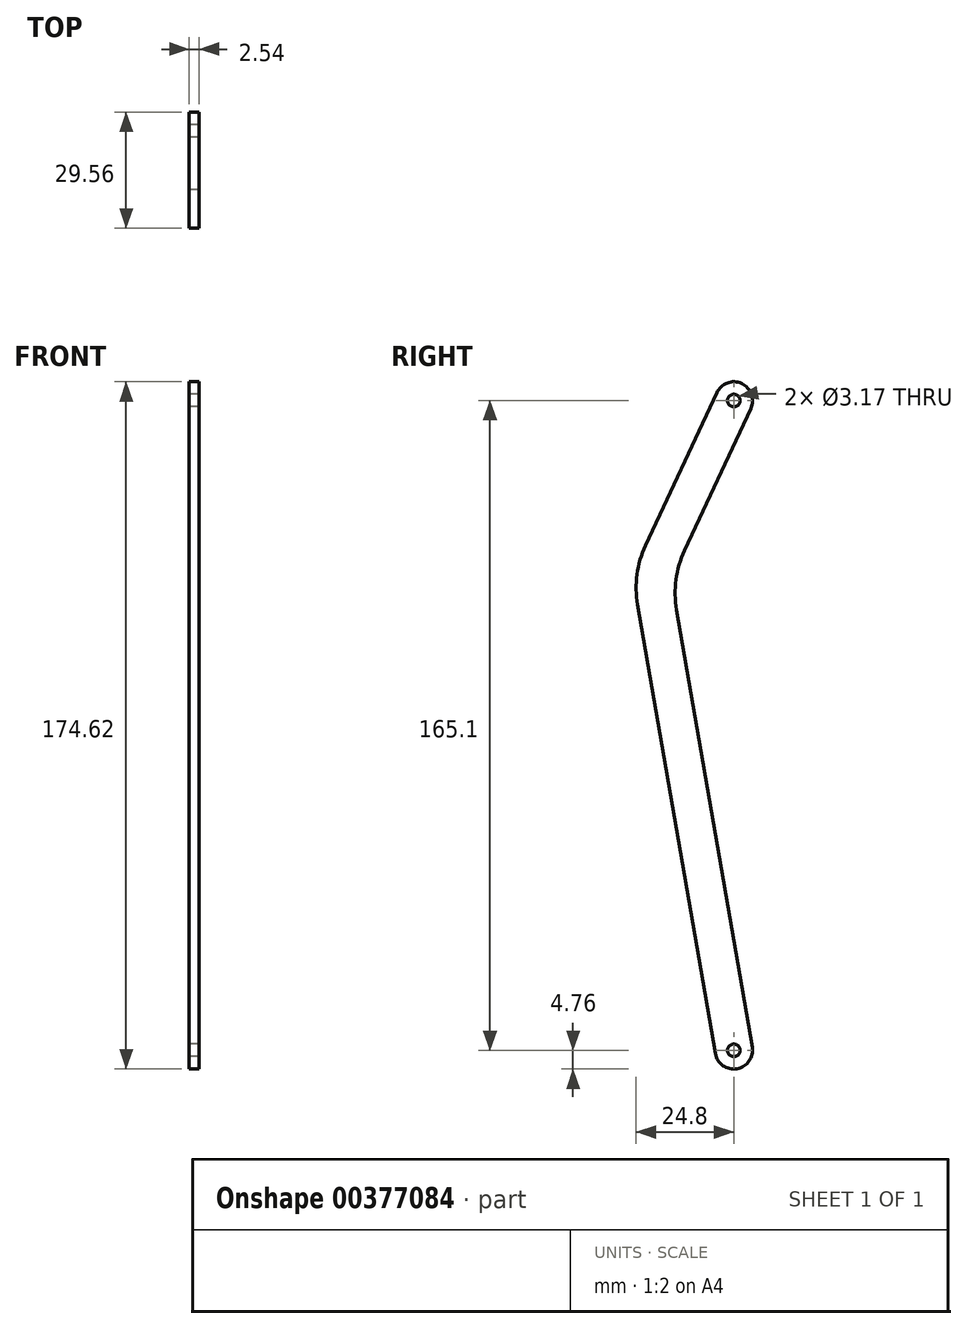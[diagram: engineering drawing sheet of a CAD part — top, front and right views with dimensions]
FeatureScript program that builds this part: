
annotation { "Feature Type Name" : "Feature", "Feature Type Description" : "" }
export const myFeature = defineFeature(function(context is Context, id is Id, definition is map)
    precondition{}
    {
        {
            var Q0;
            Q0=qCreatedBy(makeId("Right.planeOp"),FACE);
            var sketch = newSketch(context, id + "F0", { "sketchPlane" : qUnion([Q0])});
            skLineSegment(sketch, "E0", {"start": v(0, 0) * mm, "end": v(0, 165.1) * mm, "construction": true});
            skCircle(sketch, "E1", {"center": v(0, 165.1) * mm, "radius": 1.59 * mm});
            skCircle(sketch, "E2", {"center": v(0, 0) * mm, "radius": 1.59 * mm});
            skArc(sketch, "E3", {"start": v(-4.32, 167.11) * mm, "mid": v(2.01, 169.42) * mm, "end": v(4.32, 163.09) * mm});
            skArc(sketch, "E4", {"start": v(4.7, 0.81) * mm, "mid": v(0.81, -4.7) * mm, "end": v(-4.7, -0.81) * mm});
            skLineSegment(sketch, "E5", {"start": v(-4.7, -0.81) * mm, "end": v(-25.79, 121.07) * mm});
            skLineSegment(sketch, "E6", {"start": v(-25.79, 121.07) * mm, "end": v(-4.32, 167.11) * mm});
            skLineSegment(sketch, "E7", {"start": v(4.32, 163.09) * mm, "end": v(-15.9, 119.75) * mm});
            skLineSegment(sketch, "E8", {"start": v(-15.9, 119.75) * mm, "end": v(4.7, 0.81) * mm});
            skSolve(sketch);
        }
        {
            var Q0;
            Q0 = qSketchRegion(id + "F0", true);
            extrude(context, id + "F1", {"entities" : qUnion([Q0]), "depth" : 2.54 * mm});
        }
        {
            var Q0;
            Q0=makeQuery(id+"F1.opExtrude","SWEPT_EDGE",EDGE,{"disambiguationData":[OSD([sQuery(id+"F0.wireOp",EDGE,"E7"),sQuery(id+"F0.wireOp",EDGE,"E8")])]});
            var Q1;
            Q1=makeQuery(id+"F1.opExtrude","SWEPT_EDGE",EDGE,{"disambiguationData":[OSD([sQuery(id+"F0.wireOp",EDGE,"E5"),sQuery(id+"F0.wireOp",EDGE,"E6")])]});
            fillet(context, id + "F2", {"entities" : qUnion([Q0, Q1]), "radius" : 25.4 * mm, "tangentPropagation" : true, "allowEdgeOverflow" : false});
        }
    });
